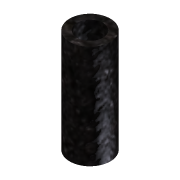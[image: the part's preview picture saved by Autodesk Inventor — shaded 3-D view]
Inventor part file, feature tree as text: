
AUTODESK INVENTOR PART (.ipt)
format: ipt  version: 2012 (Build 160160000, 160)  size: 82,432 bytes
history: native  units: mm
features: extrude x1, sketch x1
ambient origin geometry x8: Origin, YZ Plane, XZ Plane, XY Plane, X Axis, Y Axis, Z Axis, Center Point
bodies: Solid1 (feature_tree)
feature tree (2):
  extrude  "Extrusion1"  Depth=8.0mm
  sketch  "Sketch1"  dims[d0=5.1mm d1=8.0mm d2=20.4mm d3=0.0mm]
